# Revit family: ВКМц
name_source: partatom
category: Оборудование
units: mm (PartAtom-declared; Revit-internal decimal feet)

## family parameters
Всегда вертикально = Да
Классификация = Нет
На основе рабочей плоскости = Нет
Общий = Нет
При загрузке вырезать с полостями = Нет
Размер круглого соединителя = Использовать диаметр
Тип детали = Нормальный
Точка принадлежности помещению = Нет

## types (13) — shared parameters
00_20_Виробник = Вентс
00_20_Назва = Канальний відцентровий вентилятор
URL = https://vents.ua
Изготовитель = Вентс
Класифікація навантаження = HVAC
Кількість фаз = 1
Матеріал зони обслуговуваня = <По категории>
Матеріал корпусу = Сталь, гальванізована
Напруга = 230 В
Статичний тиск повітря = 0.0 Па
Частота = 50 Гц
zero-valued in all types: Отметка по умолчанию

## per-type parameters (varying)
- ВКМц 100 Б: B=253 мм; B1=293 мм; B2=213 мм; D1=237 мм; D2=212 мм; Dy=100 мм; H1=169 мм; L=202 мм; L1=23 мм; L2=22 мм; L3=30 мм; L4=62 мм; L5=41 мм; L6=87 мм; L7=40 мм; L8=92 мм; R1=119 мм; R2=124 мм; Ry=50 мм; Вага=2.50 кг; Висота=287 мм; Довжина=202 мм; Діаметр=100 мм; Потужність=42 Вт; Рівень звукового тиску на відстані 3 м=35 дБА; Струм=0 А; Установлена потужність=44 В·А; Ширина=293 мм
- ВКМц 315: B=410 мм; B1=450 мм; B2=370 мм; D1=402 мм; D2=377 мм; Dy=315 мм; H1=251 мм; L=308 мм; L1=33 мм; L2=55 мм; L3=40 мм; L4=95 мм; L5=74 мм; L6=120 мм; L7=50 мм; L8=125 мм; R1=201 мм; R2=206 мм; Ry=158 мм; Вага=6.50 кг; Висота=452 мм; Довжина=308 мм; Діаметр=315 мм; Потужність=185 Вт; Рівень звукового тиску на відстані 3 м=53 дБА; Струм=1 А; Установлена потужність=186 В·А; Ширина=450 мм
- ВКМц 100: B=253 мм; B1=293 мм; B2=213 мм; D1=237 мм; D2=212 мм; Dy=100 мм; H1=169 мм; L=202 мм; L1=23 мм; L2=22 мм; L3=30 мм; L4=62 мм; L5=41 мм; L6=87 мм; L7=40 мм; L8=92 мм; R1=119 мм; R2=124 мм; Ry=50 мм; Вага=2.80 кг; Висота=287 мм; Довжина=202 мм; Діаметр=100 мм; Потужність=62 Вт; Рівень звукового тиску на відстані 3 м=46 дБА; Струм=0 А; Установлена потужність=64 В·А; Ширина=293 мм
- ВКМц 125 Б: B=253 мм; B1=293 мм; B2=213 мм; D1=237 мм; D2=212 мм; Dy=125 мм; H1=169 мм; L=202 мм; L1=23 мм; L2=22 мм; L3=30 мм; L4=62 мм; L5=41 мм; L6=87 мм; L7=40 мм; L8=92 мм; R1=119 мм; R2=124 мм; Ry=63 мм; Вага=2.70 кг; Висота=287 мм; Довжина=202 мм; Діаметр=125 мм; Потужність=60 Вт; Рівень звукового тиску на відстані 3 м=35 дБА; Струм=0 А; Установлена потужність=85 В·А; Ширина=293 мм
- ВКМц 125: B=253 мм; B1=293 мм; B2=213 мм; D1=237 мм; D2=212 мм; Dy=125 мм; H1=169 мм; L=202 мм; L1=23 мм; L2=22 мм; L3=30 мм; L4=62 мм; L5=41 мм; L6=87 мм; L7=40 мм; L8=92 мм; R1=119 мм; R2=124 мм; Ry=63 мм; Вага=2.90 кг; Висота=287 мм; Довжина=202 мм; Діаметр=125 мм; Потужність=78 Вт; Рівень звукового тиску на відстані 3 м=46 дБА; Струм=0 А; Установлена потужність=78 В·А; Ширина=293 мм
- ВКМц 150: B=290 мм; B1=330 мм; B2=250 мм; D1=274 мм; D2=249 мм; Dy=150 мм; H1=187 мм; L=170 мм; L1=20 мм; L2=20 мм; L3=30 мм; L4=52 мм; L5=31 мм; L6=77 мм; L7=40 мм; L8=82 мм; R1=137 мм; R2=142 мм; Ry=75 мм; Вага=3.20 кг; Висота=324 мм; Довжина=170 мм; Діаметр=150 мм; Потужність=64 Вт; Рівень звукового тиску на відстані 3 м=44 дБА; Струм=0 А; Установлена потужність=67 В·А; Ширина=330 мм
- ВКМСц 150: B=355 мм; B1=395 мм; B2=315 мм; D1=345 мм; D2=320 мм; Dy=150 мм; H1=223 мм; L=230 мм; L1=20 мм; L2=20 мм; L3=40 мм; L4=82 мм; L5=61 мм; L6=107 мм; L7=50 мм; L8=112 мм; R1=173 мм; R2=178 мм; Ry=75 мм; Вага=4.80 кг; Висота=395 мм; Довжина=230 мм; Діаметр=150 мм; Потужність=127 Вт; Рівень звукового тиску на відстані 3 м=48 дБА; Струм=1 А; Установлена потужність=129 В·А; Ширина=395 мм
- ВКМц 160: B=294 мм; B1=334 мм; B2=254 мм; D1=278 мм; D2=253 мм; Dy=160 мм; H1=189 мм; L=200 мм; L1=25 мм; L2=23 мм; L3=30 мм; L4=57 мм; L5=36 мм; L6=82 мм; L7=40 мм; L8=87 мм; R1=139 мм; R2=144 мм; Ry=80 мм; Вага=3.20 кг; Висота=328 мм; Довжина=200 мм; Діаметр=160 мм; Потужність=78 Вт; Рівень звукового тиску на відстані 3 м=46 дБА; Струм=0 А; Установлена потужність=78 В·А; Ширина=334 мм
- ВКМц 200 Б: B=340 мм; B1=380 мм; B2=300 мм; D1=332 мм; D2=307 мм; Dy=200 мм; H1=216 мм; L=245 мм; L1=25 мм; L2=29 мм; L3=40 мм; L4=80 мм; L5=58 мм; L6=105 мм; L7=50 мм; L8=110 мм; R1=166 мм; R2=171 мм; Ry=100 мм; Вага=5.20 кг; Висота=382 мм; Довжина=245 мм; Діаметр=200 мм; Потужність=139 Вт; Рівень звукового тиску на відстані 3 м=48 дБА; Струм=1 А; Установлена потужність=140 В·А; Ширина=380 мм
- ВКМц 250 Б: B=340 мм; B1=380 мм; B2=300 мм; D1=332 мм; D2=307 мм; Dy=250 мм; H1=216 мм; L=213 мм; L1=25 мм; L2=29 мм; L3=40 мм; L4=64 мм; L5=42 мм; L6=89 мм; L7=50 мм; L8=94 мм; R1=166 мм; R2=171 мм; Ry=125 мм; Вага=5.10 кг; Висота=382 мм; Довжина=213 мм; Діаметр=250 мм; Потужність=134 Вт; Рівень звукового тиску на відстані 3 м=51 дБА; Струм=1 А; Установлена потужність=136 В·А; Ширина=380 мм
- ВКМц 250: B=340 мм; B1=380 мм; B2=300 мм; D1=332 мм; D2=307 мм; Dy=250 мм; H1=216 мм; L=213 мм; L1=25 мм; L2=29 мм; L3=40 мм; L4=64 мм; L5=42 мм; L6=89 мм; L7=50 мм; L8=94 мм; R1=166 мм; R2=171 мм; Ry=125 мм; Вага=5.10 кг; Висота=382 мм; Довжина=213 мм; Діаметр=250 мм; Потужність=157 Вт; Рівень звукового тиску на відстані 3 м=50 дБА; Струм=1 А; Установлена потужність=159 В·А; Ширина=380 мм
- ВКМц 315 Б: B=410 мм; B1=450 мм; B2=370 мм; D1=402 мм; D2=377 мм; Dy=315 мм; H1=251 мм; L=308 мм; L1=33 мм; L2=55 мм; L3=40 мм; L4=95 мм; L5=74 мм; L6=120 мм; L7=50 мм; L8=125 мм; R1=201 мм; R2=206 мм; Ry=158 мм; Вага=6.50 кг; Висота=452 мм; Довжина=308 мм; Діаметр=315 мм; Потужність=151 Вт; Рівень звукового тиску на відстані 3 м=52 дБА; Струм=1 А; Установлена потужність=152 В·А; Ширина=450 мм
- ВКМц 200: B=340 мм; B1=380 мм; B2=300 мм; D1=332 мм; D2=307 мм; Dy=200 мм; H1=216 мм; L=245 мм; L1=25 мм; L2=29 мм; L3=40 мм; L4=80 мм; L5=58 мм; L6=105 мм; L7=50 мм; L8=110 мм; R1=166 мм; R2=171 мм; Ry=100 мм; Вага=5.20 кг; Висота=382 мм; Довжина=245 мм; Діаметр=200 мм; Потужність=157 Вт; Рівень звукового тиску на відстані 3 м=50 дБА; Струм=1 А; Установлена потужність=159 В·А; Ширина=380 мм

note: column(s) folded — value = type name in every type: 00_20_Тип
